# Revit family: Toilet_Seat-Elongated_Closed_Front-Cleansing-KOHLER-Kohler_Novita-K-BD-N450US
name_source: partatom
category: Plumbing Fixtures
units: mm (PartAtom-declared; Revit-internal decimal feet)

## family parameters
Cut with Voids When Loaded = No
Host = Face
OmniClass Number = 23.31.19.19.17
OmniClass Title = Water Closet Seats
Part Type = Normal
Room Calculation Point = No
Round Connector Dimension = Use Diameter
Shared = No

## types (1)
- N0-White
    ADA Compliant = No
    Apparent Load = 1800 VA
    Assembly Code = C1030200
    CW Connection = Yes
    Cold Water Inlet = Cold Water Inlet
    Date Modified = 12/21/2022
    Default Elevation = 15"
    Description = Elongated Bidet Toilet Seat
    Drain Included = No
    Electrical Connector = Yes
    Electrical Note = One dedicated circuit required, protected with Class A Ground Fault Circuit-Interrupter (GFCI)
    Finish = Kohler-Plastic-0-White
    Flow Rate = 0 GPM
    HW Connection = No
    Height = 7 1/16"
    Length = 21 1/8"
    Manufacturer = Kohler Co.
    Master Format 2014 = 10 28 00
    Master Format 2014 Name = Toilet, Bath, and Laundry Accessories
    Material = Plastic
    Model = K-BD-N450US-N0
    Pressure = 80.00 psi
    Product Documentation Link = https://www.us.kohler.com
    Product Name = Kohler Novita
    Product Page URL = http://www.us.kohler.com
    Type = 1
    URL = https://www.us.kohler.com
    Vent Connection = No
    Voltage = 120 V
    Waste Connection = No
    WaterSense Certified = No
    Width = 16 7/16"

## geometry (parser evidence)
native form markers: Sweep x5
no freeform markers — native parametric forms only
